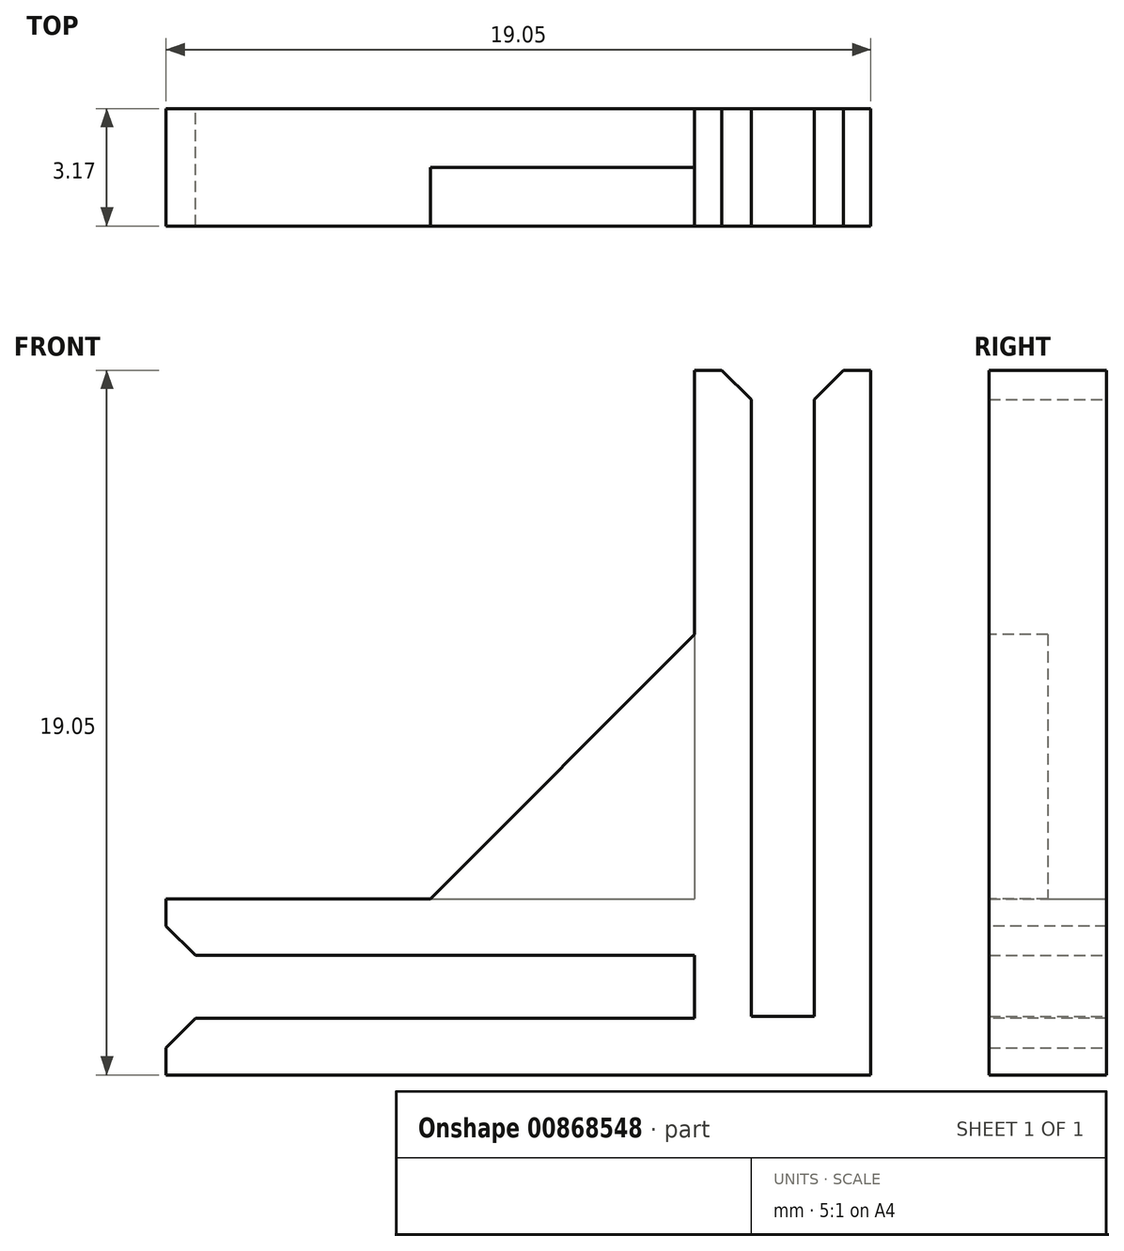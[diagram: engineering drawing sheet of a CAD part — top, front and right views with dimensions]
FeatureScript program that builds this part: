
annotation { "Feature Type Name" : "Feature", "Feature Type Description" : "" }
export const myFeature = defineFeature(function(context is Context, id is Id, definition is map)
    precondition{}
    {
        {
            var Q0;
            Q0=qCreatedBy(makeId("Front.planeOp"),FACE);
            var sketch = newSketch(context, id + "F0", { "sketchPlane" : qUnion([Q0])});
            skLineSegment(sketch, "E0.bottom", {"start": v(0, 0) * mm, "end": v(-19.05, 0) * mm});
            skLineSegment(sketch, "E0.top", {"start": v(0, 19.05) * mm, "end": v(-19.05, 19.05) * mm});
            skLineSegment(sketch, "E0.left", {"start": v(0, 0) * mm, "end": v(0, 19.05) * mm});
            skLineSegment(sketch, "E1.bottom", {"start": v(-19.05, 19.05) * mm, "end": v(-4.76, 19.05) * mm});
            skLineSegment(sketch, "E1.top", {"start": v(-19.05, 4.76) * mm, "end": v(-4.76, 4.76) * mm});
            skLineSegment(sketch, "E1.left", {"start": v(-19.05, 19.05) * mm, "end": v(-19.05, 4.76) * mm});
            skLineSegment(sketch, "E1.right", {"start": v(-4.76, 19.05) * mm, "end": v(-4.76, 4.76) * mm});
            skLineSegment(sketch, "E2.top", {"start": v(-19.05, 3.23) * mm, "end": v(-3.23, 3.23) * mm});
            skLineSegment(sketch, "E2.right", {"start": v(-3.23, 19.05) * mm, "end": v(-3.23, 3.23) * mm});
            skLineSegment(sketch, "E3.top", {"start": v(-19.05, 1.53) * mm, "end": v(-1.53, 1.53) * mm});
            skLineSegment(sketch, "E3.right", {"start": v(-1.53, 19.05) * mm, "end": v(-1.53, 1.53) * mm});
            skLineSegment(sketch, "E4.bottom", {"start": v(0, 0) * mm, "end": v(-4.76, 0) * mm});
            skLineSegment(sketch, "E4.top", {"start": v(0, 7.94) * mm, "end": v(-4.76, 7.94) * mm});
            skLineSegment(sketch, "E4.left", {"start": v(0, 0) * mm, "end": v(0, 7.94) * mm});
            skLineSegment(sketch, "E4.right", {"start": v(-4.76, 0) * mm, "end": v(-4.76, 7.94) * mm});
            skLineSegment(sketch, "E5.bottom", {"start": v(0, 0) * mm, "end": v(-7.94, 0) * mm});
            skLineSegment(sketch, "E5.top", {"start": v(0, 4.76) * mm, "end": v(-7.94, 4.76) * mm});
            skLineSegment(sketch, "E5.left", {"start": v(0, 0) * mm, "end": v(0, 4.76) * mm});
            skLineSegment(sketch, "E5.right", {"start": v(-7.94, 0) * mm, "end": v(-7.94, 4.76) * mm});
            skLineSegment(sketch, "E6", {"start": v(-4.76, 19.05) * mm, "end": v(-3.23, 19.05) * mm});
            skLineSegment(sketch, "E7", {"start": v(-3.23, 19.05) * mm, "end": v(-1.53, 19.05) * mm});
            skLineSegment(sketch, "E8", {"start": v(-1.53, 19.05) * mm, "end": v(0, 19.05) * mm});
            skLineSegment(sketch, "E9", {"start": v(-19.05, 4.76) * mm, "end": v(-19.05, 3.23) * mm});
            skLineSegment(sketch, "E10", {"start": v(-19.05, 3.23) * mm, "end": v(-19.05, 1.53) * mm});
            skLineSegment(sketch, "E11", {"start": v(-19.05, 1.53) * mm, "end": v(-19.05, 0) * mm});
            skSolve(sketch);
        }
        {
            var Q0;
            {var subQ0=sQuery(id+"F0.wireOp",EDGE,"E3.right");var subQ1=sQuery(id+"F0.wireOp",EDGE,"E0.top");var subQ2=makeQuery(id+"F0.imprint","INTERSECT",VERTEX,{"derivedFrom":[subQ1,subQ0]});Q0=makeQuery(id+"F0.imprint","IMPRINT",FACE,{"disambiguationData":[TD([[makeQuery(id+"F0.imprint","IMPRINT",EDGE,{"disambiguationData":[TD([[subQ2,1.0]])],"derivedFrom":subQ1}),1.0]])]});}
            var Q1;
            {var subQ0=sQuery(id+"F0.wireOp",EDGE,"E1.right");var subQ1=sQuery(id+"F0.wireOp",EDGE,"E0.top");var subQ2=makeQuery(id+"F0.imprint","INTERSECT",VERTEX,{"derivedFrom":[subQ1,subQ0]});Q1=makeQuery(id+"F0.imprint","IMPRINT",FACE,{"disambiguationData":[TD([[makeQuery(id+"F0.imprint","IMPRINT",EDGE,{"disambiguationData":[TD([[subQ2,1.0]])],"derivedFrom":subQ1}),1.0]])]});}
            var Q2;
            {var subQ0=sQuery(id+"F0.wireOp",EDGE,"E4.top");var subQ1=sQuery(id+"F0.wireOp",EDGE,"E0.left");var subQ2=makeQuery(id+"F0.imprint","INTERSECT",VERTEX,{"derivedFrom":[subQ1,subQ0]});Q2=makeQuery(id+"F0.imprint","IMPRINT",FACE,{"disambiguationData":[TD([[makeQuery(id+"F0.imprint","IMPRINT",EDGE,{"disambiguationData":[TD([[subQ2,1.0]])],"derivedFrom":subQ1}),1.0]])]});}
            var Q3;
            {var subQ0=sQuery(id+"F0.wireOp",EDGE,"E4.top");var subQ1=sQuery(id+"F0.wireOp",EDGE,"E2.right");var subQ2=makeQuery(id+"F0.imprint","INTERSECT",VERTEX,{"derivedFrom":[subQ1,subQ0]});Q3=makeQuery(id+"F0.imprint","IMPRINT",FACE,{"disambiguationData":[TD([[makeQuery(id+"F0.imprint","IMPRINT",EDGE,{"disambiguationData":[TD([[subQ2,-1.0]])],"derivedFrom":subQ1}),1.0]])]});}
            var Q4;
            {var subQ3=sQuery(id+"F0.wireOp",EDGE,"E4.top");var subQ5=sQuery(id+"F0.wireOp",EDGE,"E2.right");var subQ6=makeQuery(id+"F0.imprint","INTERSECT",VERTEX,{"derivedFrom":[subQ5,subQ3]});Q4=makeQuery(id+"F0.imprint","IMPRINT",FACE,{"disambiguationData":[TD([[makeQuery(id+"F0.imprint","IMPRINT",EDGE,{"disambiguationData":[TD([[subQ6,-1.0]])],"derivedFrom":subQ5}),-1.0]])]});}
            var Q5;
            {var subQ7=sQuery(id+"F0.wireOp",EDGE,"E0.left");var subQ8=sQuery(id+"F0.wireOp",EDGE,"E0.bottom");var subQ9=makeQuery(id+"F0.imprint","INTERSECT",VERTEX,{"derivedFrom":[subQ8,subQ7]});Q5=makeQuery(id+"F0.imprint","IMPRINT",FACE,{"disambiguationData":[TD([[makeQuery(id+"F0.imprint","IMPRINT",EDGE,{"disambiguationData":[TD([[subQ9,-1.0]])],"derivedFrom":subQ8}),-1.0]])]});}
            var Q6;
            {var subQ5=sQuery(id+"F0.wireOp",EDGE,"E2.right");var subQ6=sQuery(id+"F0.wireOp",EDGE,"E2.top");var subQ7=makeQuery(id+"F0.imprint","INTERSECT",VERTEX,{"derivedFrom":[subQ6,subQ5]});Q6=makeQuery(id+"F0.imprint","IMPRINT",FACE,{"disambiguationData":[TD([[makeQuery(id+"F0.imprint","IMPRINT",EDGE,{"disambiguationData":[TD([[subQ7,1.0]])],"derivedFrom":subQ6}),-1.0]])]});}
            var Q7;
            {var subQ0=sQuery(id+"F0.wireOp",EDGE,"E2.right");var subQ1=sQuery(id+"F0.wireOp",EDGE,"E2.top");var subQ2=makeQuery(id+"F0.imprint","INTERSECT",VERTEX,{"derivedFrom":[subQ1,subQ0]});Q7=makeQuery(id+"F0.imprint","IMPRINT",FACE,{"disambiguationData":[TD([[makeQuery(id+"F0.imprint","IMPRINT",EDGE,{"disambiguationData":[TD([[subQ2,1.0]])],"derivedFrom":subQ1}),1.0]])]});}
            var Q8;
            {var subQ0=sQuery(id+"F0.wireOp",EDGE,"E9");Q8=makeQuery(id+"F0.imprint","IMPRINT",FACE,{"disambiguationData":[TD([[makeQuery(id+"F0.imprint","IMPRINT",EDGE,{"derivedFrom":subQ0}),1.0]])]});}
            var Q9;
            {var subQ3=sQuery(id+"F0.wireOp",EDGE,"E11");Q9=makeQuery(id+"F0.imprint","IMPRINT",FACE,{"disambiguationData":[TD([[makeQuery(id+"F0.imprint","IMPRINT",EDGE,{"derivedFrom":subQ3}),1.0]])]});}
            var Q10;
            {var subQ0=sQuery(id+"F0.wireOp",EDGE,"E5.right");var subQ1=sQuery(id+"F0.wireOp",EDGE,"E0.bottom");var subQ2=makeQuery(id+"F0.imprint","INTERSECT",VERTEX,{"derivedFrom":[subQ1,subQ0]});Q10=makeQuery(id+"F0.imprint","IMPRINT",FACE,{"disambiguationData":[TD([[makeQuery(id+"F0.imprint","IMPRINT",EDGE,{"disambiguationData":[TD([[subQ2,1.0]])],"derivedFrom":subQ1}),-1.0]])]});}
            var Q11;
            {var subQ0=sQuery(id+"F0.wireOp",EDGE,"E5.right");var subQ1=sQuery(id+"F0.wireOp",EDGE,"E2.top");var subQ2=makeQuery(id+"F0.imprint","INTERSECT",VERTEX,{"derivedFrom":[subQ1,subQ0]});Q11=makeQuery(id+"F0.imprint","IMPRINT",FACE,{"disambiguationData":[TD([[makeQuery(id+"F0.imprint","IMPRINT",EDGE,{"disambiguationData":[TD([[subQ2,-1.0]])],"derivedFrom":subQ1}),-1.0]])]});}
            var Q12;
            {var subQ3=sQuery(id+"F0.wireOp",EDGE,"E5.right");var subQ5=sQuery(id+"F0.wireOp",EDGE,"E2.top");var subQ6=makeQuery(id+"F0.imprint","INTERSECT",VERTEX,{"derivedFrom":[subQ5,subQ3]});Q12=makeQuery(id+"F0.imprint","IMPRINT",FACE,{"disambiguationData":[TD([[makeQuery(id+"F0.imprint","IMPRINT",EDGE,{"disambiguationData":[TD([[subQ6,-1.0]])],"derivedFrom":subQ5}),1.0]])]});}
            extrude(context, id + "F1", {"entities" : qUnion([Q0, Q1, Q2, Q3, Q4, Q5, Q6, Q7, Q8, Q9, Q10, Q11, Q12]), "depth" : 3.17 * mm, "offsetDistance" : 25.4 * mm});
        }
        {
            var Q0;
            Q0=makeQuery(id+"F1.opExtrude","CAP_FACE",FACE,{"disambiguationData":[OSD([sQuery(id+"F0.wireOp",EDGE,"E0.bottom"),sQuery(id+"F0.wireOp",EDGE,"E0.top"),sQuery(id+"F0.wireOp",EDGE,"E0.left"),sQuery(id+"F0.wireOp",EDGE,"E1.top"),sQuery(id+"F0.wireOp",EDGE,"E1.right"),sQuery(id+"F0.wireOp",EDGE,"E2.top"),sQuery(id+"F0.wireOp",EDGE,"E2.right"),sQuery(id+"F0.wireOp",EDGE,"E3.top"),sQuery(id+"F0.wireOp",EDGE,"E3.right"),sQuery(id+"F0.wireOp",EDGE,"E4.top"),sQuery(id+"F0.wireOp",EDGE,"E5.right"),sQuery(id+"F0.wireOp",EDGE,"E9"),sQuery(id+"F0.wireOp",EDGE,"E11")])],"isStart":false});
            var sketch = newSketch(context, id + "F2", { "sketchPlane" : qUnion([Q0])});
            skLineSegment(sketch, "E12", {"start": v(-11.9, 4.76) * mm, "end": v(-4.76, 11.9) * mm});
            skLineSegment(sketch, "E13", {"start": v(-4.76, 11.9) * mm, "end": v(-4.76, 4.76) * mm});
            skLineSegment(sketch, "E14", {"start": v(-4.76, 4.76) * mm, "end": v(-11.9, 4.76) * mm});
            skSolve(sketch);
        }
        {
            var Q0;
            Q0=makeQuery(id+"F2.imprint","IMPRINT",FACE,{"disambiguationData":[TD([[makeQuery(id+"F2.imprint","IMPRINT",EDGE,{"derivedFrom":sQuery(id+"F2.wireOp",EDGE,"E12")}),-1.0]])]});
            extrude(context, id + "F3", {"entities" : qUnion([Q0]), "operationType" : NewBodyOperationType.ADD, "oppositeDirection" : true, "depth" : 1.59 * mm, "offsetDistance" : 25.4 * mm});
        }
        {
            var Q0;
            Q0=makeQuery(id+"F1.opExtrude","SWEPT_EDGE",EDGE,{"disambiguationData":[OSD([sQuery(id+"F0.wireOp",EDGE,"E2.top"),sQuery(id+"F0.wireOp",EDGE,"E9"),sQuery(id+"F0.wireOp",EDGE,"E10")])]});
            var Q1;
            Q1=makeQuery(id+"F1.opExtrude","SWEPT_EDGE",EDGE,{"disambiguationData":[OSD([sQuery(id+"F0.wireOp",EDGE,"E3.top"),sQuery(id+"F0.wireOp",EDGE,"E10"),sQuery(id+"F0.wireOp",EDGE,"E11")])]});
            var Q2;
            Q2=makeQuery(id+"F1.opExtrude","SWEPT_EDGE",EDGE,{"disambiguationData":[OSD([sQuery(id+"F0.wireOp",EDGE,"E0.top"),sQuery(id+"F0.wireOp",EDGE,"E3.right")])]});
            var Q3;
            Q3=makeQuery(id+"F1.opExtrude","SWEPT_EDGE",EDGE,{"disambiguationData":[OSD([sQuery(id+"F0.wireOp",EDGE,"E0.top"),sQuery(id+"F0.wireOp",EDGE,"E2.right")])]});
            chamfer(context, id + "F4", {"entities" : qUnion([Q0, Q1, Q2, Q3]), "width" : 0.8 * mm, "tangentPropagation" : true});
        }
        {
            var Q0;
            Q0=makeQuery(id+"F1.opExtrude","SWEPT_FACE",FACE,{"disambiguationData":[OSD([sQuery(id+"F0.wireOp",EDGE,"E4.top")])]});
            extrude(context, id + "F5", {"entities" : qUnion([Q0]), "operationType" : NewBodyOperationType.REMOVE, "oppositeDirection" : true, "depth" : 6.35 * mm, "offsetDistance" : 25.4 * mm});
        }
        {
            var Q0;
            Q0=makeQuery(id+"F1.opExtrude","SWEPT_FACE",FACE,{"disambiguationData":[OSD([sQuery(id+"F0.wireOp",EDGE,"E5.right")])]});
            extrude(context, id + "F6", {"entities" : qUnion([Q0]), "operationType" : NewBodyOperationType.REMOVE, "oppositeDirection" : true, "depth" : 3.17 * mm, "offsetDistance" : 25.4 * mm});
        }
    });
